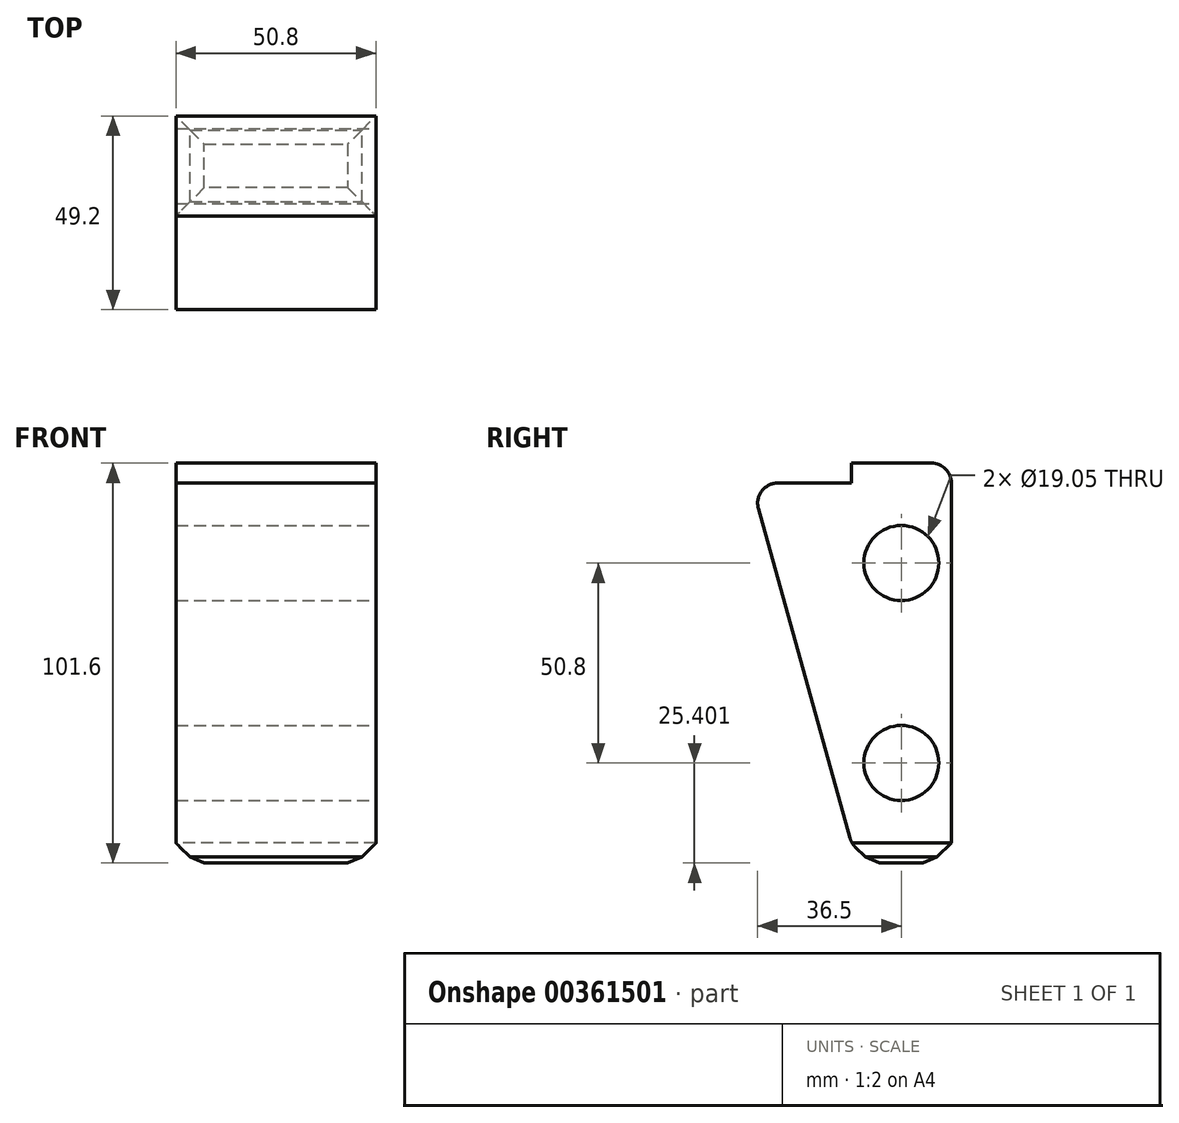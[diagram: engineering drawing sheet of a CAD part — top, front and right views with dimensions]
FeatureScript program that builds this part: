
annotation { "Feature Type Name" : "Feature", "Feature Type Description" : "" }
export const myFeature = defineFeature(function(context is Context, id is Id, definition is map)
    precondition{}
    {
        {
            var Q0;
            Q0=qCreatedBy(makeId("Front.planeOp"),FACE);
            var sketch = newSketch(context, id + "F0", { "sketchPlane" : qUnion([Q0])});
            skLineSegment(sketch, "E0.bottom", {"start": v(-4.7, 40.38) * mm, "end": v(46.1, 40.38) * mm});
            skLineSegment(sketch, "E0.top", {"start": v(-4.7, -61.22) * mm, "end": v(46.1, -61.22) * mm});
            skLineSegment(sketch, "E0.left", {"start": v(-4.7, 40.38) * mm, "end": v(-4.7, -61.22) * mm});
            skLineSegment(sketch, "E0.right", {"start": v(46.1, 40.38) * mm, "end": v(46.1, -61.22) * mm});
            skSolve(sketch);
        }
        {
            var Q0;
            Q0 = qSketchRegion(id + "F0", true);
            extrude(context, id + "F1", {"entities" : qUnion([Q0]), "depth" : 25.4 * mm});
        }
        {
            var Q0;
            Q0=makeQuery(id+"F1.opExtrude","SWEPT_FACE",FACE,{"disambiguationData":[OSD([sQuery(id+"F0.wireOp",EDGE,"E0.right")])]});
            var sketch = newSketch(context, id + "F2", { "sketchPlane" : qUnion([Q0])});
            skCircle(sketch, "E1", {"center": v(-12.7, 14.98) * mm, "radius": 9.53 * mm});
            skCircle(sketch, "E2", {"center": v(-12.7, -35.82) * mm, "radius": 9.53 * mm});
            skSolve(sketch);
        }
        {
            var Q0;
            Q0 = qSketchRegion(id + "F2", true);
            extrude(context, id + "F3", {"entities" : qUnion([Q0]), "operationType" : NewBodyOperationType.REMOVE, "oppositeDirection" : true, "depth" : 50.8 * mm});
        }
        {
            var Q0;
            Q0=makeQuery(id+"F1.opExtrude","SWEPT_FACE",FACE,{"disambiguationData":[OSD([sQuery(id+"F0.wireOp",EDGE,"E0.top")])]});
            var Q1;
            Q1=makeQuery(id+"F1.opExtrude","CAP_EDGE",EDGE,{"disambiguationData":[OSD([sQuery(id+"F0.wireOp",EDGE,"E0.top")])],"isStart":false});
            chamfer(context, id + "F4", {"entities" : qUnion([Q0, Q1]), "width" : 5.08 * mm, "tangentPropagation" : true});
        }
        {
            var Q0;
            Q0=makeQuery(id+"F1.opExtrude","SWEPT_FACE",FACE,{"disambiguationData":[OSD([sQuery(id+"F0.wireOp",EDGE,"E0.top")])]});
            chamfer(context, id + "F5", {"entities" : qUnion([Q0]), "width" : 5.08 * mm, "tangentPropagation" : true});
        }
        {
            var Q0;
            Q0=makeQuery(id+"F1.opExtrude","SWEPT_FACE",FACE,{"disambiguationData":[OSD([sQuery(id+"F0.wireOp",EDGE,"E0.left")])]});
            var sketch = newSketch(context, id + "F6", { "sketchPlane" : qUnion([Q0])});
            skLineSegment(sketch, "E3", {"start": v(25.4, 35.3) * mm, "end": v(50.8, 35.3) * mm});
            skLineSegment(sketch, "E4", {"start": v(50.8, 35.3) * mm, "end": v(25.4, -56.14) * mm});
            skSolve(sketch);
        }
        {
            var Q0;
            Q0=makeQuery(id+"F6.imprint","IMPRINT",FACE,{"disambiguationData":[TD([[makeQuery(id+"F6.imprint","IMPRINT",EDGE,{"derivedFrom":sQuery(id+"F6.wireOp",EDGE,"E3")}),-1.0]])]});
            extrude(context, id + "F7", {"entities" : qUnion([Q0]), "operationType" : NewBodyOperationType.ADD, "oppositeDirection" : true, "depth" : 50.8 * mm});
        }
        {
            var Q0;
            Q0=makeQuery(id+"F7.opExtrude","SWEPT_EDGE",EDGE,{"disambiguationData":[OSD([sQuery(id+"F6.wireOp",EDGE,"E3"),sQuery(id+"F6.wireOp",EDGE,"E4")])]});
            var Q1;
            Q1=makeQuery(id+"F1.opExtrude","CAP_EDGE",EDGE,{"disambiguationData":[OSD([sQuery(id+"F0.wireOp",EDGE,"E0.bottom")])],"isStart":true});
            var Q2;
            {var subQ0=sQuery(id+"F0.wireOp",EDGE,"E0.left");var subQ1=sQuery(id+"F0.wireOp",EDGE,"E0.top");Q2=makeQuery(id+"F7.boolean.opBoolean","MERGE",EDGE,{"derivedFrom":[makeQuery(id+"F5.opChamfer","BLEND_EDGE",EDGE,{"blendedFrom":[makeQuery(id+"F1.opExtrude","CAP_EDGE",EDGE,{"disambiguationData":[OSD([subQ1])],"isStart":false}),makeQuery(id+"F1.opExtrude","CAP_FACE",FACE,{"disambiguationData":[OSD([sQuery(id+"F0.wireOp",EDGE,"E0.bottom"),subQ1,subQ0,sQuery(id+"F0.wireOp",EDGE,"E0.right")])],"isStart":false})],"blendedInto":[makeQuery(id+"F1.opExtrude","CAP_FACE",FACE,{"disambiguationData":[OSD([sQuery(id+"F0.wireOp",EDGE,"E0.bottom"),subQ1,subQ0,sQuery(id+"F0.wireOp",EDGE,"E0.right")])],"isStart":false})]}),makeQuery(id+"F7.opExtrude","SWEPT_EDGE",EDGE,{"disambiguationData":[OSD([subQ1,subQ0,sQuery(id+"F6.wireOp",EDGE,"E4")])]})]});}
            var Q3;
            {var subQ0=sQuery(id+"F0.wireOp",EDGE,"E0.top");Q3=makeQuery(id+"F5.opChamfer","BLEND_EDGE",EDGE,{"blendedFrom":[makeQuery(id+"F1.opExtrude","CAP_EDGE",EDGE,{"disambiguationData":[OSD([subQ0])],"isStart":true}),makeQuery(id+"F1.opExtrude","CAP_FACE",FACE,{"disambiguationData":[OSD([sQuery(id+"F0.wireOp",EDGE,"E0.bottom"),subQ0,sQuery(id+"F0.wireOp",EDGE,"E0.left"),sQuery(id+"F0.wireOp",EDGE,"E0.right")])],"isStart":true})],"blendedInto":[makeQuery(id+"F1.opExtrude","CAP_FACE",FACE,{"disambiguationData":[OSD([sQuery(id+"F0.wireOp",EDGE,"E0.bottom"),subQ0,sQuery(id+"F0.wireOp",EDGE,"E0.left"),sQuery(id+"F0.wireOp",EDGE,"E0.right")])],"isStart":true})]});}
            fillet(context, id + "F8", {"entities" : qUnion([Q0, Q1, Q2, Q3]), "radius" : 5.08 * mm, "tangentPropagation" : true, "allowEdgeOverflow" : false});
        }
    });
